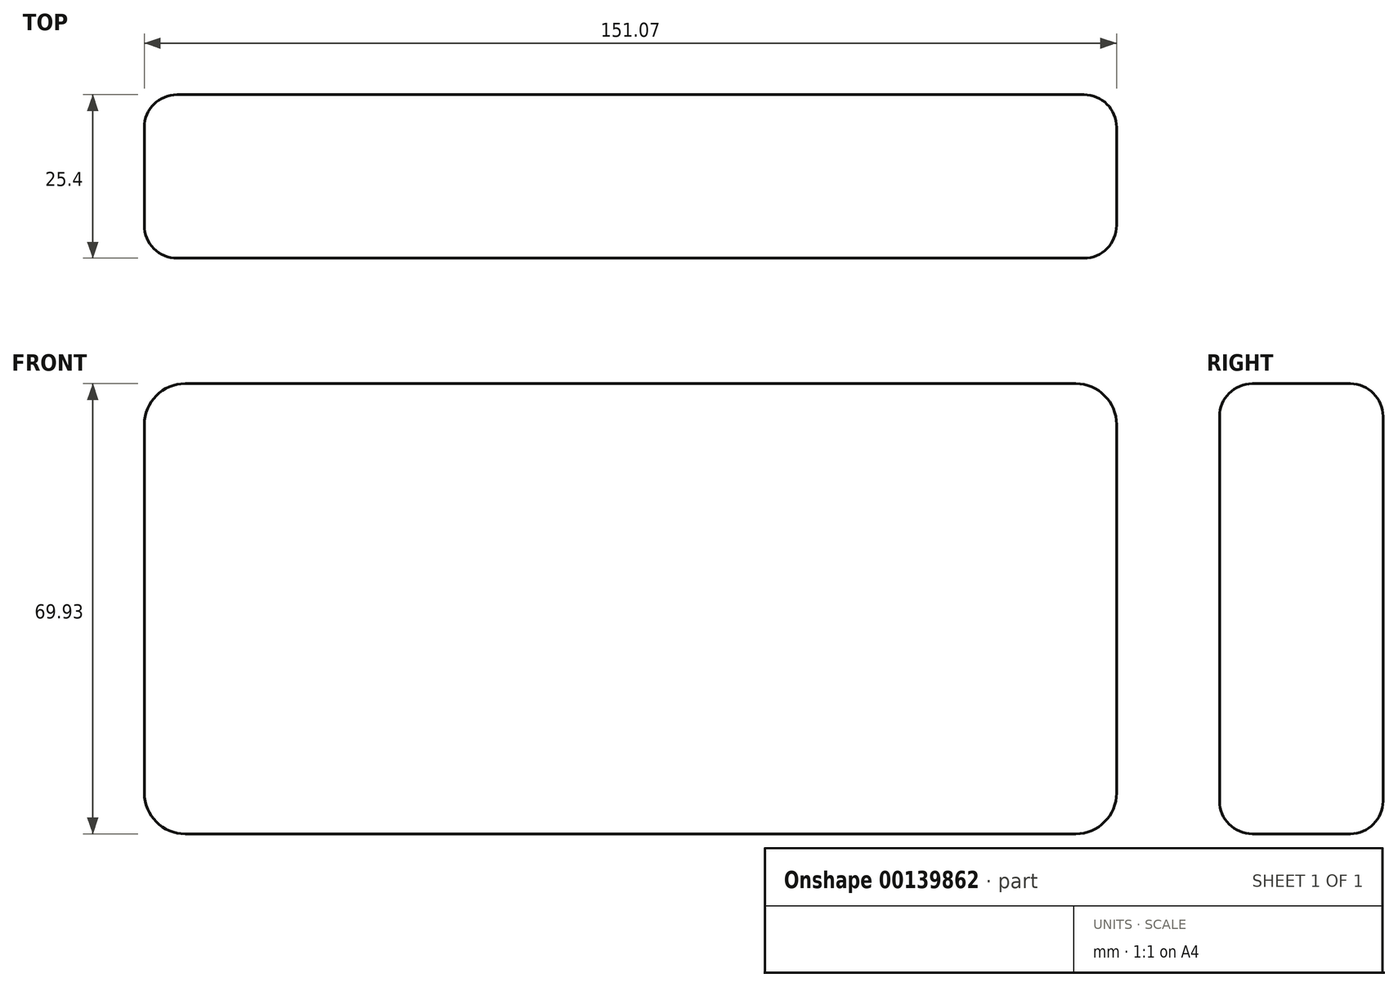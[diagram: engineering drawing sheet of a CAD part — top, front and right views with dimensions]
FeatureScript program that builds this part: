
annotation { "Feature Type Name" : "Feature", "Feature Type Description" : "" }
export const myFeature = defineFeature(function(context is Context, id is Id, definition is map)
    precondition{}
    {
        {
            var Q0;
            Q0=qCreatedBy(makeId("Front.planeOp"),FACE);
            var sketch = newSketch(context, id + "F0", { "sketchPlane" : qUnion([Q0])});
            skLineSegment(sketch, "E0.bottom", {"start": v(-6.35, 0) * mm, "end": v(-144.72, 0) * mm});
            skLineSegment(sketch, "E0.top", {"start": v(-6.35, 69.93) * mm, "end": v(-144.72, 69.93) * mm});
            skLineSegment(sketch, "E0.left", {"start": v(0, 6.35) * mm, "end": v(0, 63.58) * mm});
            skLineSegment(sketch, "E0.right", {"start": v(-151.07, 6.35) * mm, "end": v(-151.07, 63.58) * mm});
            skPoint(sketch, "E1.visualSharp", {"position": v(0, 0) * mm});
            skArc(sketch, "E1.filletArc", {"start": v(-6.35, 0) * mm, "mid": v(-1.86, 1.86) * mm, "end": v(0, 6.35) * mm});
            skPoint(sketch, "E2.visualSharp", {"position": v(0, 69.93) * mm});
            skArc(sketch, "E2.filletArc", {"start": v(0, 63.58) * mm, "mid": v(-1.86, 68.07) * mm, "end": v(-6.35, 69.93) * mm});
            skPoint(sketch, "E3.visualSharp", {"position": v(-151.07, 0) * mm});
            skArc(sketch, "E3.filletArc", {"start": v(-151.07, 6.35) * mm, "mid": v(-149.2, 1.86) * mm, "end": v(-144.72, 0) * mm});
            skPoint(sketch, "E4.visualSharp", {"position": v(-151.07, 69.93) * mm});
            skArc(sketch, "E4.filletArc", {"start": v(-144.72, 69.93) * mm, "mid": v(-149.2, 68.07) * mm, "end": v(-151.07, 63.58) * mm});
            skSolve(sketch);
        }
        {
            var Q0;
            Q0 = qSketchRegion(id + "F0", true);
            var Q1;
            Q1=makeQuery(id+"F0.imprint","IMPRINT",FACE,{"disambiguationData":[TD([[makeQuery(id+"F0.imprint","IMPRINT",EDGE,{"derivedFrom":sQuery(id+"F0.wireOp",EDGE,"E0.bottom")}),-1.0]])]});
            extrude(context, id + "F1", {"entities" : qUnion([Q0, Q1]), "depth" : 25.4 * mm});
        }
        {
            var Q0;
            Q0=makeQuery(id+"F1.opExtrude","CAP_EDGE",EDGE,{"disambiguationData":[OSD([sQuery(id+"F0.wireOp",EDGE,"E0.right")])],"isStart":true});
            var Q1;
            Q1=makeQuery(id+"F1.opExtrude","CAP_EDGE",EDGE,{"disambiguationData":[OSD([sQuery(id+"F0.wireOp",EDGE,"E0.right")])],"isStart":false});
            fillet(context, id + "F2", {"entities" : qUnion([Q0, Q1]), "radius" : 5.08 * mm, "tangentPropagation" : true, "allowEdgeOverflow" : false});
        }
    });
